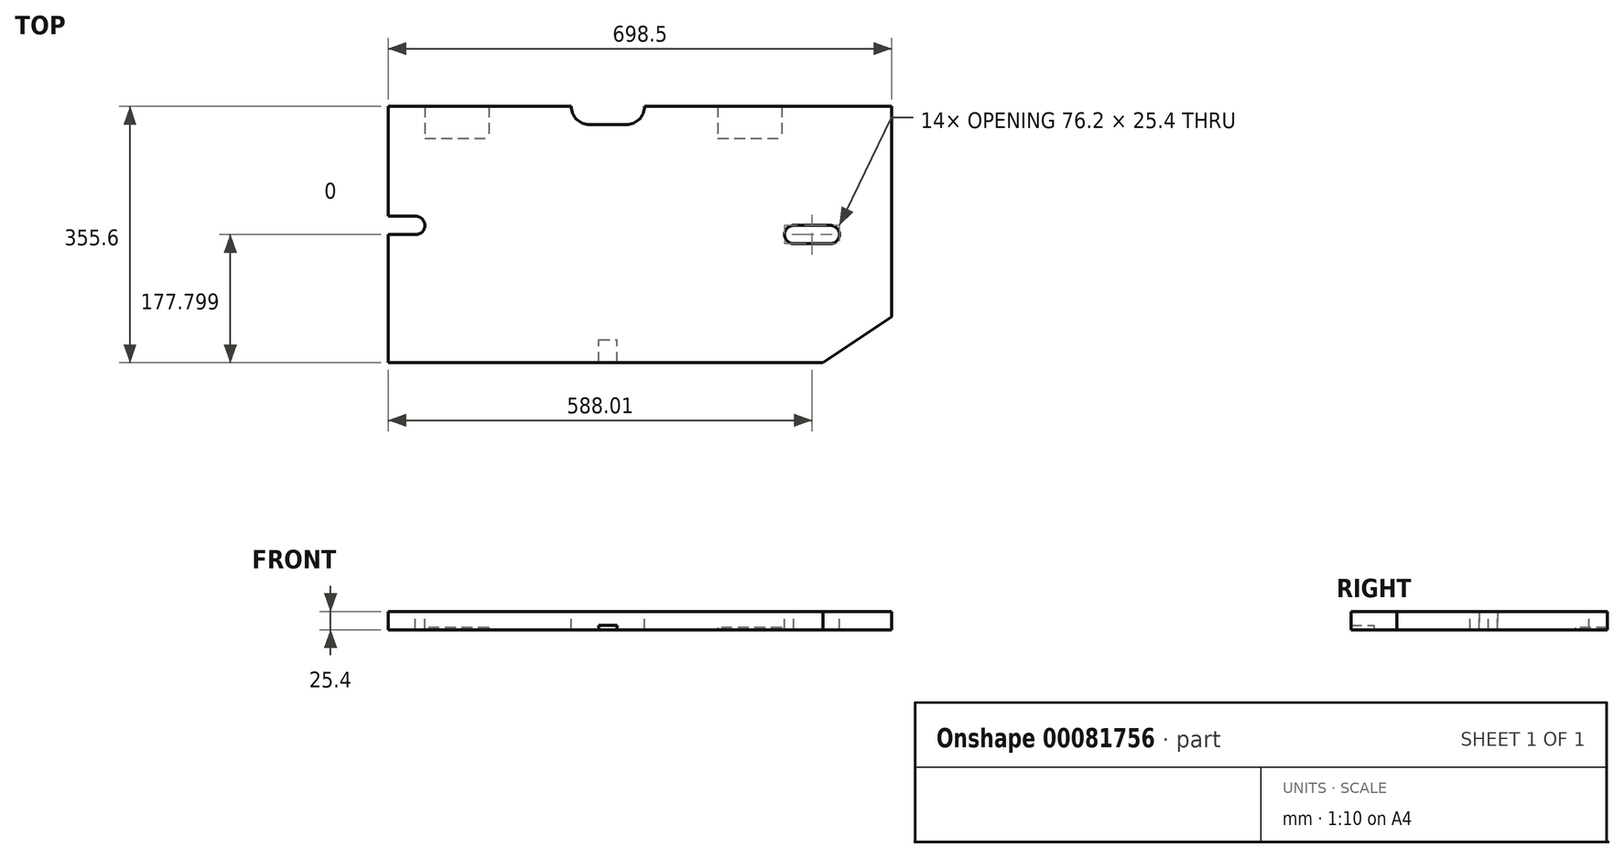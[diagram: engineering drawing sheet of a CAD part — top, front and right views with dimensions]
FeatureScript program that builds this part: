
annotation { "Feature Type Name" : "Feature", "Feature Type Description" : "" }
export const myFeature = defineFeature(function(context is Context, id is Id, definition is map)
    precondition{}
    {
        {
            var Q0;
            Q0=qCreatedBy(makeId("Top.planeOp"),FACE);
            var sketch = newSketch(context, id + "F0", { "sketchPlane" : qUnion([Q0])});
            skLineSegment(sketch, "E0.bottom", {"start": v(349.25, -177.8) * mm, "end": v(-349.25, -177.8) * mm});
            skLineSegment(sketch, "E0.top", {"start": v(349.25, 177.8) * mm, "end": v(-349.25, 177.8) * mm});
            skLineSegment(sketch, "E0.left", {"start": v(349.25, -177.8) * mm, "end": v(349.25, 177.8) * mm});
            skLineSegment(sketch, "E0.right", {"start": v(-349.25, -177.8) * mm, "end": v(-349.25, 177.8) * mm});
            skPoint(sketch, "E0.middle", {"position": v(0, 0) * mm});
            skSolve(sketch);
        }
        {
            var Q0;
            Q0 = qSketchRegion(id + "F0", true);
            extrude(context, id + "F1", {"entities" : qUnion([Q0]), "depth" : 25.4 * mm});
        }
        {
            var Q0;
            Q0=makeQuery(id+"F1.opExtrude","CAP_FACE",FACE,{"disambiguationData":[OSD([sQuery(id+"F0.wireOp",EDGE,"E0.bottom"),sQuery(id+"F0.wireOp",EDGE,"E0.top"),sQuery(id+"F0.wireOp",EDGE,"E0.left"),sQuery(id+"F0.wireOp",EDGE,"E0.right")])],"isStart":false});
            var sketch = newSketch(context, id + "F2", { "sketchPlane" : qUnion([Q0])});
            skLineSegment(sketch, "E1", {"start": v(254, -177.8) * mm, "end": v(349.25, -114.3) * mm});
            skLineSegment(sketch, "E2", {"start": v(349.25, -114.3) * mm, "end": v(349.25, -177.8) * mm});
            skLineSegment(sketch, "E3", {"start": v(349.25, -177.8) * mm, "end": v(254, -177.8) * mm});
            skSolve(sketch);
        }
        {
            var Q0;
            Q0 = qSketchRegion(id + "F2", true);
            extrude(context, id + "F3", {"entities" : qUnion([Q0]), "operationType" : NewBodyOperationType.REMOVE, "endBound" : BoundingType.THROUGH_ALL, "oppositeDirection" : true, "depth" : 25.4 * mm});
        }
        {
            var Q0;
            Q0=makeQuery(id+"F1.opExtrude","CAP_FACE",FACE,{"disambiguationData":[OSD([sQuery(id+"F0.wireOp",EDGE,"E0.bottom"),sQuery(id+"F0.wireOp",EDGE,"E0.top"),sQuery(id+"F0.wireOp",EDGE,"E0.left"),sQuery(id+"F0.wireOp",EDGE,"E0.right")])],"isStart":true});
            var sketch = newSketch(context, id + "F4", { "sketchPlane" : qUnion([Q0])});
            skLineSegment(sketch, "E4.bottom", {"start": v(-298.45, -177.8) * mm, "end": v(-209.55, -177.8) * mm});
            skLineSegment(sketch, "E4.top", {"start": v(-298.45, -133.35) * mm, "end": v(-209.55, -133.35) * mm});
            skLineSegment(sketch, "E4.left", {"start": v(-298.45, -177.8) * mm, "end": v(-298.45, -133.35) * mm});
            skLineSegment(sketch, "E4.right", {"start": v(-209.55, -177.8) * mm, "end": v(-209.55, -133.35) * mm});
            skLineSegment(sketch, "E5.bottom", {"start": v(107.95, -177.8) * mm, "end": v(196.85, -177.8) * mm});
            skLineSegment(sketch, "E5.top", {"start": v(107.95, -133.35) * mm, "end": v(196.85, -133.35) * mm});
            skLineSegment(sketch, "E5.left", {"start": v(107.95, -177.8) * mm, "end": v(107.95, -133.35) * mm});
            skLineSegment(sketch, "E5.right", {"start": v(196.85, -177.8) * mm, "end": v(196.85, -133.35) * mm});
            skSolve(sketch);
        }
        {
            var Q0;
            Q0 = qSketchRegion(id + "F4", true);
            extrude(context, id + "F5", {"entities" : qUnion([Q0]), "operationType" : NewBodyOperationType.REMOVE, "oppositeDirection" : true, "depth" : 3.17 * mm});
        }
        {
            var Q0;
            Q0=makeQuery(id+"F1.opExtrude","CAP_FACE",FACE,{"disambiguationData":[OSD([sQuery(id+"F0.wireOp",EDGE,"E0.bottom"),sQuery(id+"F0.wireOp",EDGE,"E0.top"),sQuery(id+"F0.wireOp",EDGE,"E0.left"),sQuery(id+"F0.wireOp",EDGE,"E0.right")])],"isStart":false});
            var sketch = newSketch(context, id + "F6", { "sketchPlane" : qUnion([Q0])});
            skArc(sketch, "E6", {"start": v(-311.75, 0.01) * mm, "mid": v(-298.45, 12.7) * mm, "end": v(-311.75, 25.39) * mm});
            skLineSegment(sketch, "E7.bottom", {"start": v(-311.75, 25.39) * mm, "end": v(-382.24, 25.39) * mm});
            skLineSegment(sketch, "E7.top", {"start": v(-311.75, 0) * mm, "end": v(-382.24, 0) * mm});
            skLineSegment(sketch, "E7.left", {"start": v(-311.75, 0.01) * mm, "end": v(-311.75, 0) * mm});
            skLineSegment(sketch, "E7.right", {"start": v(-382.24, 25.39) * mm, "end": v(-382.24, 0) * mm});
            skArc(sketch, "E8", {"start": v(213.52, 12.7) * mm, "mid": v(200.66, 0) * mm, "end": v(213.52, -12.7) * mm});
            skLineSegment(sketch, "E9.bottom", {"start": v(213.52, 12.7) * mm, "end": v(264.16, 12.7) * mm});
            skLineSegment(sketch, "E9.top", {"start": v(213.52, -12.7) * mm, "end": v(264.16, -12.7) * mm});
            skLineSegment(sketch, "E9.left", {"start": v(213.52, -12.7) * mm, "end": v(213.52, -12.7) * mm});
            skArc(sketch, "E10", {"start": v(264.16, -12.7) * mm, "mid": v(276.86, 0) * mm, "end": v(264.16, 12.7) * mm});
            skSolve(sketch);
        }
        {
            var Q0;
            Q0 = qSketchRegion(id + "F6", true);
            extrude(context, id + "F7", {"entities" : qUnion([Q0]), "operationType" : NewBodyOperationType.REMOVE, "endBound" : BoundingType.THROUGH_ALL, "oppositeDirection" : true, "depth" : 25.4 * mm});
        }
        {
            var Q0;
            Q0=makeQuery(id+"F1.opExtrude","CAP_FACE",FACE,{"disambiguationData":[OSD([sQuery(id+"F0.wireOp",EDGE,"E0.bottom"),sQuery(id+"F0.wireOp",EDGE,"E0.top"),sQuery(id+"F0.wireOp",EDGE,"E0.left"),sQuery(id+"F0.wireOp",EDGE,"E0.right")])],"isStart":false});
            var sketch = newSketch(context, id + "F8", { "sketchPlane" : qUnion([Q0])});
            skLineSegment(sketch, "E11.bottom", {"start": v(-95.25, 177.8) * mm, "end": v(6.35, 177.8) * mm});
            skLineSegment(sketch, "E11.top", {"start": v(-95.25, 152.4) * mm, "end": v(6.35, 152.4) * mm});
            skLineSegment(sketch, "E11.left", {"start": v(-95.25, 177.8) * mm, "end": v(-95.25, 152.4) * mm});
            skLineSegment(sketch, "E11.right", {"start": v(6.35, 177.8) * mm, "end": v(6.35, 152.4) * mm});
            skSolve(sketch);
        }
        {
            var Q0;
            Q0 = qSketchRegion(id + "F8", true);
            extrude(context, id + "F9", {"entities" : qUnion([Q0]), "operationType" : NewBodyOperationType.REMOVE, "oppositeDirection" : true, "depth" : 25.4 * mm});
        }
        {
            var Q0;
            Q0=makeQuery(id+"F9.boolean.opBoolean","COPY",EDGE,{"derivedFrom":makeQuery(id+"F9.opExtrude","SWEPT_EDGE",EDGE,{"disambiguationData":[OSD([sQuery(id+"F8.wireOp",EDGE,"E11.top"),sQuery(id+"F8.wireOp",EDGE,"E11.left")])]})});
            var Q1;
            Q1=makeQuery(id+"F9.boolean.opBoolean","COPY",EDGE,{"derivedFrom":makeQuery(id+"F9.opExtrude","SWEPT_EDGE",EDGE,{"disambiguationData":[OSD([sQuery(id+"F8.wireOp",EDGE,"E11.top"),sQuery(id+"F8.wireOp",EDGE,"E11.right")])]})});
            var Q2;
            Q2=makeQuery(id+"F9.boolean.opBoolean","COPY",EDGE,{"derivedFrom":makeQuery(id+"F9.opExtrude","SWEPT_EDGE",EDGE,{"disambiguationData":[OSD([sQuery(id+"F8.wireOp",EDGE,"wrKPGfHQ-pwjH-arrm-bZTW-P1KEAwDJg62S.top"),sQuery(id+"F8.wireOp",EDGE,"wrKPGfHQ-pwjH-arrm-bZTW-P1KEAwDJg62S.left")])]})});
            var Q3;
            Q3=makeQuery(id+"F9.boolean.opBoolean","COPY",EDGE,{"derivedFrom":makeQuery(id+"F9.opExtrude","SWEPT_EDGE",EDGE,{"disambiguationData":[OSD([sQuery(id+"F8.wireOp",EDGE,"wrKPGfHQ-pwjH-arrm-bZTW-P1KEAwDJg62S.top"),sQuery(id+"F8.wireOp",EDGE,"wrKPGfHQ-pwjH-arrm-bZTW-P1KEAwDJg62S.right")])]})});
            fillet(context, id + "F10", {"entities" : qUnion([Q0, Q1, Q2, Q3]), "radius" : 25.4 * mm, "tangentPropagation" : true, "allowEdgeOverflow" : false});
        }
        {
            var Q0;
            Q0=makeQuery(id+"F1.opExtrude","CAP_FACE",FACE,{"disambiguationData":[OSD([sQuery(id+"F0.wireOp",EDGE,"E0.bottom"),sQuery(id+"F0.wireOp",EDGE,"E0.top"),sQuery(id+"F0.wireOp",EDGE,"E0.left"),sQuery(id+"F0.wireOp",EDGE,"E0.right")])],"isStart":true});
            var sketch = newSketch(context, id + "F11", { "sketchPlane" : qUnion([Q0])});
            skLineSegment(sketch, "E12.bottom", {"start": v(-57.15, 177.8) * mm, "end": v(-31.75, 177.8) * mm});
            skLineSegment(sketch, "E12.top", {"start": v(-57.15, 146.05) * mm, "end": v(-31.75, 146.05) * mm});
            skLineSegment(sketch, "E12.left", {"start": v(-57.15, 177.8) * mm, "end": v(-57.15, 146.05) * mm});
            skLineSegment(sketch, "E12.right", {"start": v(-31.75, 177.8) * mm, "end": v(-31.75, 146.05) * mm});
            skSolve(sketch);
        }
        {
            var Q0;
            Q0 = qSketchRegion(id + "F11", true);
            extrude(context, id + "F12", {"entities" : qUnion([Q0]), "operationType" : NewBodyOperationType.REMOVE, "oppositeDirection" : true, "depth" : 6.35 * mm});
        }
    });
